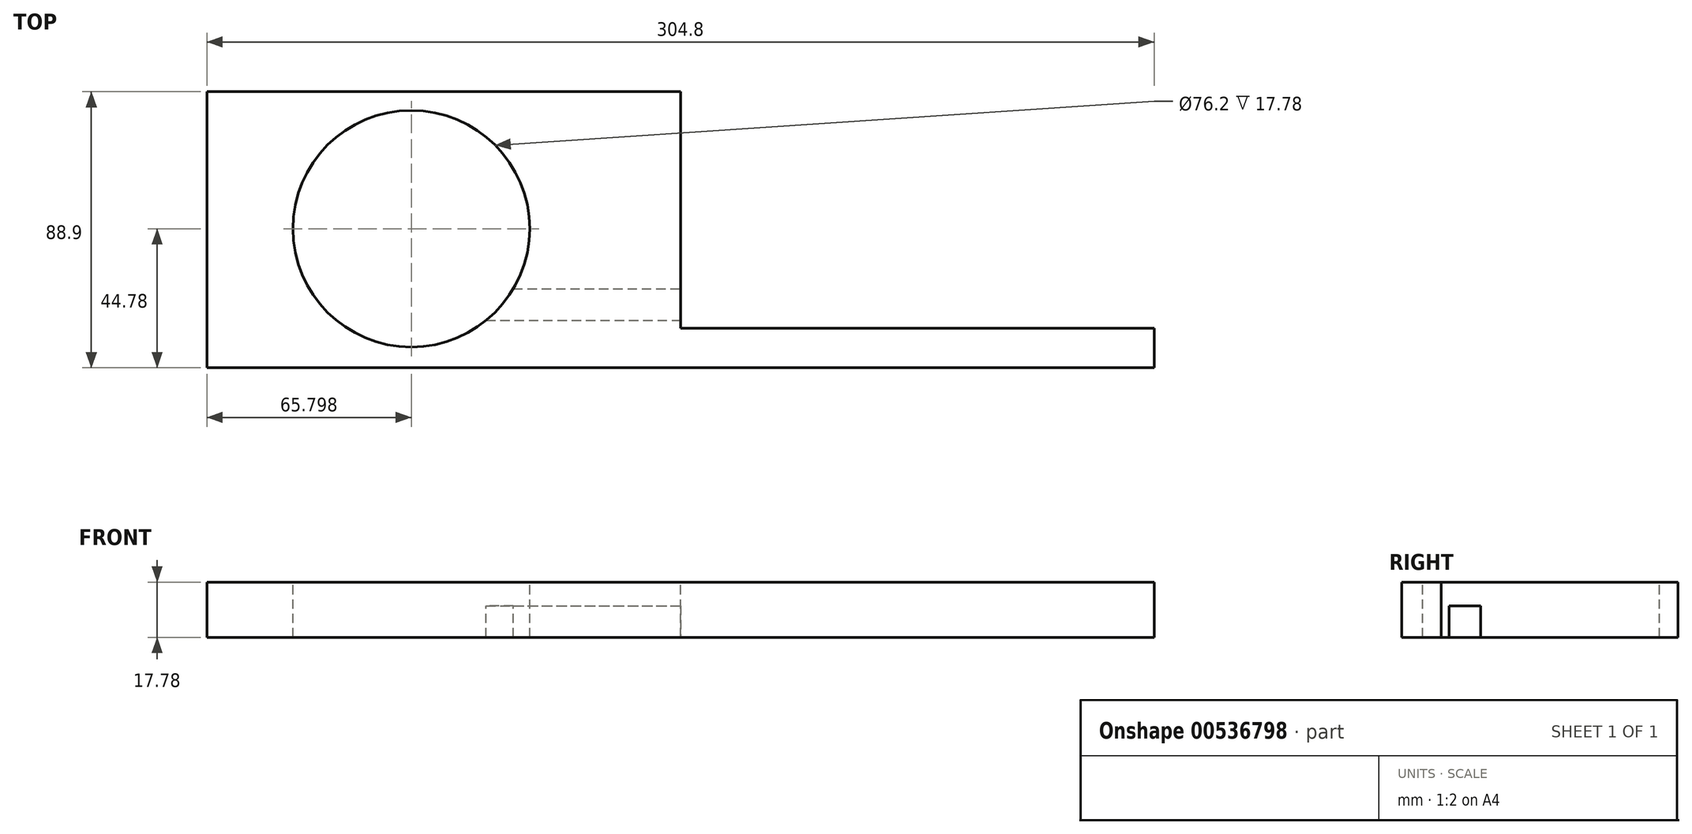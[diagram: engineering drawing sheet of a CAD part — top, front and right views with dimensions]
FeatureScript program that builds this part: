
annotation { "Feature Type Name" : "Feature", "Feature Type Description" : "" }
export const myFeature = defineFeature(function(context is Context, id is Id, definition is map)
    precondition{}
    {
        {
            var Q0;
            Q0=qCreatedBy(makeId("Top.planeOp"),FACE);
            var sketch = newSketch(context, id + "F0", { "sketchPlane" : qUnion([Q0])});
            skLineSegment(sketch, "E0.bottom", {"start": v(-217.82, 44.12) * mm, "end": v(86.98, 44.12) * mm});
            skLineSegment(sketch, "E0.top", {"start": v(-217.82, -44.78) * mm, "end": v(86.98, -44.78) * mm});
            skLineSegment(sketch, "E0.left", {"start": v(-217.82, 44.12) * mm, "end": v(-217.82, -44.78) * mm});
            skLineSegment(sketch, "E0.right", {"start": v(86.98, 44.12) * mm, "end": v(86.98, -44.78) * mm});
            skSolve(sketch);
        }
        {
            var Q0;
            Q0=makeQuery(id+"F0.imprint","IMPRINT",FACE,{"disambiguationData":[TD([[makeQuery(id+"F0.imprint","IMPRINT",EDGE,{"derivedFrom":sQuery(id+"F0.wireOp",EDGE,"E0.bottom")}),-1.0]])]});
            extrude(context, id + "F1", {"entities" : qUnion([Q0]), "depth" : 17.78 * mm, "offsetDistance" : 25.4 * mm});
        }
        {
            var Q0;
            Q0=makeQuery(id+"F1.opExtrude","CAP_FACE",FACE,{"disambiguationData":[OSD([sQuery(id+"F0.wireOp",EDGE,"E0.bottom"),sQuery(id+"F0.wireOp",EDGE,"E0.top"),sQuery(id+"F0.wireOp",EDGE,"E0.left"),sQuery(id+"F0.wireOp",EDGE,"E0.right")])],"isStart":false});
            var sketch = newSketch(context, id + "F2", { "sketchPlane" : qUnion([Q0])});
            skLineSegment(sketch, "E1.bottom", {"start": v(86.98, 44.12) * mm, "end": v(-65.42, 44.12) * mm});
            skLineSegment(sketch, "E1.top", {"start": v(86.98, -32.08) * mm, "end": v(-65.42, -32.08) * mm});
            skLineSegment(sketch, "E1.left", {"start": v(86.98, 44.12) * mm, "end": v(86.98, -32.08) * mm});
            skLineSegment(sketch, "E1.right", {"start": v(-65.42, 44.12) * mm, "end": v(-65.42, -32.08) * mm});
            skSolve(sketch);
        }
        {
            var Q0;
            Q0 = qSketchRegion(id + "F2", true);
            extrude(context, id + "F3", {"entities" : qUnion([Q0]), "operationType" : NewBodyOperationType.REMOVE, "oppositeDirection" : true, "depth" : 25.4 * mm, "offsetDistance" : 25.4 * mm});
        }
        {
            var Q0;
            Q0=makeQuery(id+"F1.opExtrude","CAP_FACE",FACE,{"disambiguationData":[OSD([sQuery(id+"F0.wireOp",EDGE,"E0.bottom"),sQuery(id+"F0.wireOp",EDGE,"E0.top"),sQuery(id+"F0.wireOp",EDGE,"E0.left"),sQuery(id+"F0.wireOp",EDGE,"E0.right")])],"isStart":false});
            var sketch = newSketch(context, id + "F4", { "sketchPlane" : qUnion([Q0])});
            skCircle(sketch, "E2", {"center": v(-152.02, 0) * mm, "radius": 38.1 * mm});
            skSolve(sketch);
        }
        {
            var Q0;
            Q0=makeQuery(id+"F4.imprint","IMPRINT",FACE,{"disambiguationData":[TD([[makeQuery(id+"F4.imprint","IMPRINT",EDGE,{"derivedFrom":sQuery(id+"F4.wireOp",EDGE,"E2")}),1.0]])]});
            extrude(context, id + "F5", {"entities" : qUnion([Q0]), "operationType" : NewBodyOperationType.REMOVE, "oppositeDirection" : true, "depth" : 25.4 * mm, "offsetDistance" : 25.4 * mm});
        }
        {
            var Q0;
            Q0=qCreatedBy(makeId("Right.planeOp"),FACE);
            var sketch = newSketch(context, id + "F6", { "sketchPlane" : qUnion([Q0])});
            skLineSegment(sketch, "E3.bottom", {"start": v(-29.56, 0) * mm, "end": v(-19.4, 0) * mm});
            skLineSegment(sketch, "E3.top", {"start": v(-29.56, 10.16) * mm, "end": v(-19.4, 10.16) * mm});
            skLineSegment(sketch, "E3.left", {"start": v(-29.56, 0) * mm, "end": v(-29.56, 10.16) * mm});
            skLineSegment(sketch, "E3.right", {"start": v(-19.4, 0) * mm, "end": v(-19.4, 10.16) * mm});
            skSolve(sketch);
        }
        {
            var Q0;
            Q0=makeQuery(id+"F6.imprint","IMPRINT",FACE,{"disambiguationData":[TD([[makeQuery(id+"F6.imprint","IMPRINT",EDGE,{"derivedFrom":sQuery(id+"F6.wireOp",EDGE,"E3.bottom")}),1.0]])]});
            var Q1;
            Q1=makeQuery(id+"F5.boolean.opBoolean","COPY",FACE,{"derivedFrom":makeQuery(id+"F5.opExtrude","SWEPT_FACE",FACE,{"disambiguationData":[OSD([sQuery(id+"F4.wireOp",EDGE,"E2")])]})});
            extrude(context, id + "F7", {"entities" : qUnion([Q0]), "operationType" : NewBodyOperationType.REMOVE, "endBound" : BoundingType.UP_TO_SURFACE, "oppositeDirection" : true, "depth" : 25.4 * mm, "endBoundEntityFace" : qUnion([Q1]), "offsetDistance" : 25.4 * mm});
        }
    });
